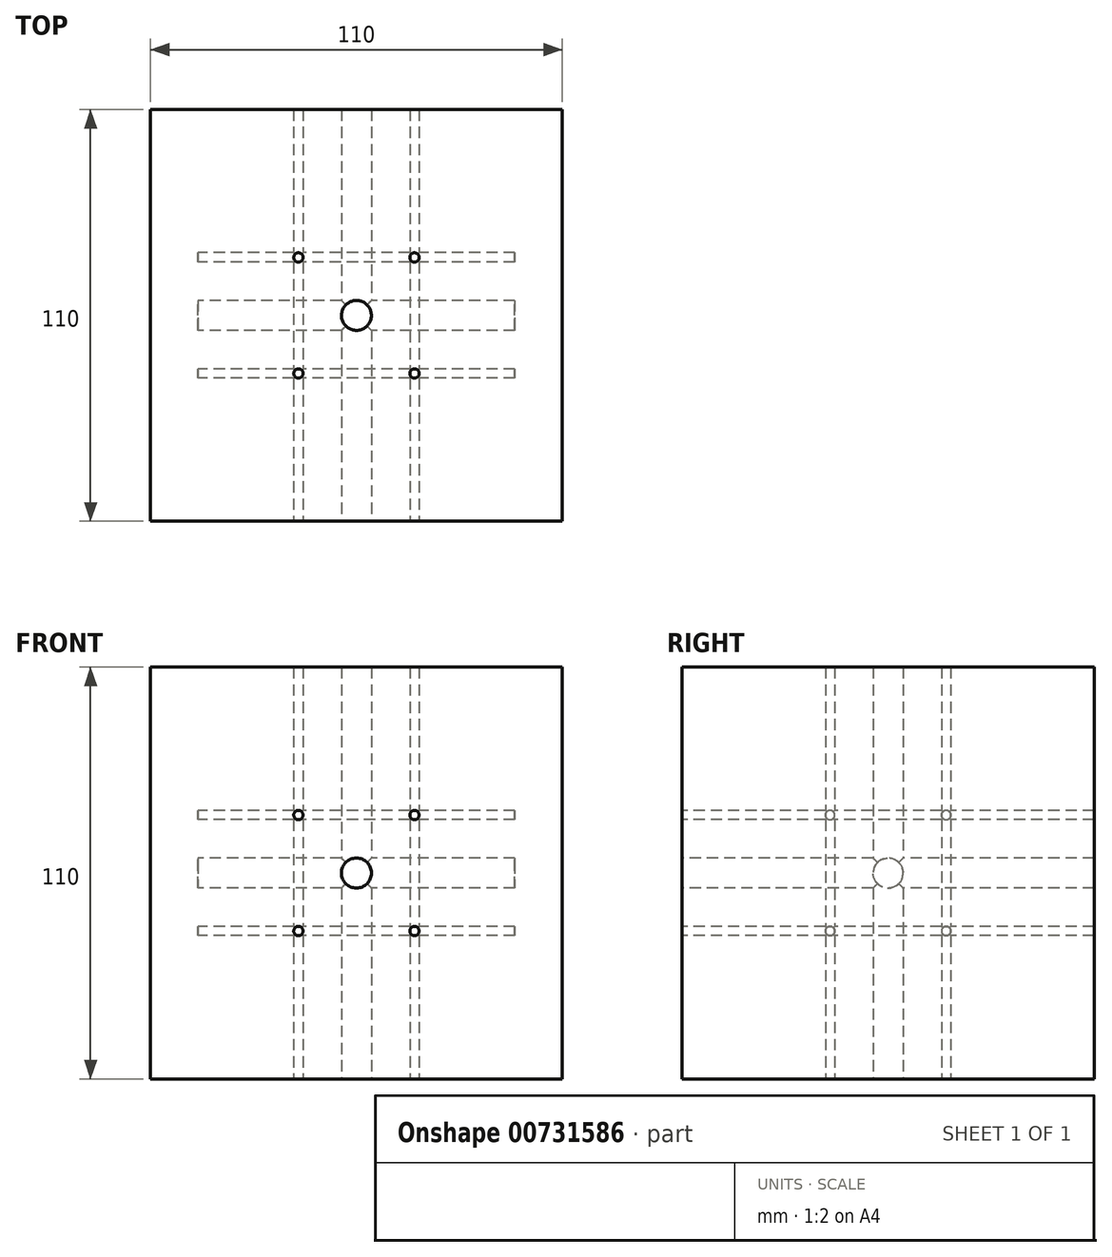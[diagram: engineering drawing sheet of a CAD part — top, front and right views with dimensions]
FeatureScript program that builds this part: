
annotation { "Feature Type Name" : "Feature", "Feature Type Description" : "" }
export const myFeature = defineFeature(function(context is Context, id is Id, definition is map)
    precondition{}
    {
        {
            assignVariable(context, id + "F0", {"name" : "MOT", "anyValue" : 42.3});
        }
        {
            var Q0;
            Q0=qCreatedBy(makeId("Top.planeOp"),FACE);
            var sketch = newSketch(context, id + "F1", { "sketchPlane" : qUnion([Q0])});
            skCircle(sketch, "E0.0", {"center": v(-15.5, 15.5) * mm, "radius": 1.25 * mm});
            skCircle(sketch, "E0.1", {"center": v(-15.5, -15.5) * mm, "radius": 1.25 * mm});
            skCircle(sketch, "E0.2", {"center": v(15.5, -15.5) * mm, "radius": 1.25 * mm});
            skCircle(sketch, "E0.3", {"center": v(15.5, 15.5) * mm, "radius": 1.25 * mm});
            skCircle(sketch, "E1", {"center": v(0, 0) * mm, "radius": 21.92 * mm, "construction": true});
            skLineSegment(sketch, "E2.bottom", {"start": v(55, 55) * mm, "end": v(-55, 55) * mm});
            skLineSegment(sketch, "E2.top", {"start": v(55, -55) * mm, "end": v(-55, -55) * mm});
            skLineSegment(sketch, "E2.left", {"start": v(55, 55) * mm, "end": v(55, -55) * mm});
            skLineSegment(sketch, "E2.right", {"start": v(-55, 55) * mm, "end": v(-55, -55) * mm});
            skLineSegment(sketch, "E3.bottom", {"start": v(21.15, 21.15) * mm, "end": v(-21.15, 21.15) * mm, "construction": true});
            skLineSegment(sketch, "E3.top", {"start": v(21.15, -21.15) * mm, "end": v(-21.15, -21.15) * mm, "construction": true});
            skLineSegment(sketch, "E3.left", {"start": v(21.15, 21.15) * mm, "end": v(21.15, -21.15) * mm, "construction": true});
            skLineSegment(sketch, "E3.right", {"start": v(-21.15, 21.15) * mm, "end": v(-21.15, -21.15) * mm, "construction": true});
            skCircle(sketch, "E4", {"center": v(0, 0) * mm, "radius": 55 * mm, "construction": true});
            skCircle(sketch, "E5", {"center": v(0, 0) * mm, "radius": 21.15 * mm, "construction": true});
            skCircle(sketch, "E6", {"center": v(0, 0) * mm, "radius": 4 * mm});
            skLineSegment(sketch, "E7", {"start": v(-75.61, 0) * mm, "end": v(74.32, 0) * mm, "construction": true});
            skSolve(sketch);
        }
        {
            var Q0;
            Q0=makeQuery(id+"F1.imprint","IMPRINT",FACE,{"disambiguationData":[TD([[makeQuery(id+"F1.imprint","IMPRINT",EDGE,{"derivedFrom":sQuery(id+"F1.wireOp",EDGE,"E0.0")}),-1.0]])]});
            extrude(context, id + "F2", {"entities" : qUnion([Q0]), "depth" : 110 * mm, "offsetDistance" : 25 * mm, "symmetric" : true});
        }
        {
            var Q0;
            Q0=qCreatedBy(makeId("Front.planeOp"),FACE);
            var sketch = newSketch(context, id + "F3", { "sketchPlane" : qUnion([Q0])});
            skCircle(sketch, "E8.0", {"center": v(-15.5, 15.5) * mm, "radius": 1.25 * mm});
            skCircle(sketch, "E8.1", {"center": v(-15.5, -15.5) * mm, "radius": 1.25 * mm});
            skCircle(sketch, "E8.2", {"center": v(15.5, -15.5) * mm, "radius": 1.25 * mm});
            skCircle(sketch, "E8.3", {"center": v(15.5, 15.5) * mm, "radius": 1.25 * mm});
            skCircle(sketch, "E9", {"center": v(0, 0) * mm, "radius": 21.92 * mm, "construction": true});
            skLineSegment(sketch, "E10.bottom", {"start": v(27.5, 27.5) * mm, "end": v(-27.5, 27.5) * mm});
            skLineSegment(sketch, "E10.top", {"start": v(27.5, -27.5) * mm, "end": v(-27.5, -27.5) * mm});
            skLineSegment(sketch, "E10.left", {"start": v(27.5, 27.5) * mm, "end": v(27.5, -27.5) * mm});
            skLineSegment(sketch, "E10.right", {"start": v(-27.5, 27.5) * mm, "end": v(-27.5, -27.5) * mm});
            skLineSegment(sketch, "E11.bottom", {"start": v(21.15, 21.15) * mm, "end": v(-21.15, 21.15) * mm, "construction": true});
            skLineSegment(sketch, "E11.top", {"start": v(21.15, -21.15) * mm, "end": v(-21.15, -21.15) * mm, "construction": true});
            skLineSegment(sketch, "E11.left", {"start": v(21.15, 21.15) * mm, "end": v(21.15, -21.15) * mm, "construction": true});
            skLineSegment(sketch, "E11.right", {"start": v(-21.15, 21.15) * mm, "end": v(-21.15, -21.15) * mm, "construction": true});
            skCircle(sketch, "E12", {"center": v(0, 0) * mm, "radius": 27.5 * mm, "construction": true});
            skCircle(sketch, "E13", {"center": v(0, 0) * mm, "radius": 21.15 * mm, "construction": true});
            skCircle(sketch, "E14", {"center": v(0, 0) * mm, "radius": 4 * mm});
            skLineSegment(sketch, "E15", {"start": v(-75.61, 0) * mm, "end": v(74.32, 0) * mm, "construction": true});
            skSolve(sketch);
        }
        {
            var Q0;
            Q0=makeQuery(id+"F3.imprint","IMPRINT",FACE,{"disambiguationData":[TD([[makeQuery(id+"F3.imprint","IMPRINT",EDGE,{"derivedFrom":sQuery(id+"F3.wireOp",EDGE,"E8.3")}),1.0]])]});
            var Q1;
            Q1=makeQuery(id+"F3.imprint","IMPRINT",FACE,{"disambiguationData":[TD([[makeQuery(id+"F3.imprint","IMPRINT",EDGE,{"derivedFrom":sQuery(id+"F3.wireOp",EDGE,"E14")}),1.0]])]});
            var Q2;
            Q2=makeQuery(id+"F3.imprint","IMPRINT",FACE,{"disambiguationData":[TD([[makeQuery(id+"F3.imprint","IMPRINT",EDGE,{"derivedFrom":sQuery(id+"F3.wireOp",EDGE,"E8.0")}),1.0]])]});
            var Q3;
            Q3=makeQuery(id+"F3.imprint","IMPRINT",FACE,{"disambiguationData":[TD([[makeQuery(id+"F3.imprint","IMPRINT",EDGE,{"derivedFrom":sQuery(id+"F3.wireOp",EDGE,"E8.1")}),1.0]])]});
            var Q4;
            Q4=makeQuery(id+"F3.imprint","IMPRINT",FACE,{"disambiguationData":[TD([[makeQuery(id+"F3.imprint","IMPRINT",EDGE,{"derivedFrom":sQuery(id+"F3.wireOp",EDGE,"E8.2")}),1.0]])]});
            extrude(context, id + "F4", {"entities" : qUnion([Q0, Q1, Q2, Q3, Q4]), "operationType" : NewBodyOperationType.REMOVE, "endBound" : BoundingType.THROUGH_ALL, "oppositeDirection" : true, "depth" : (getVariable(context, 'MOT') * 2) * mm, "offsetDistance" : 25 * mm, "hasSecondDirection" : true, "secondDirectionBound" : BoundingType.THROUGH_ALL, "secondDirectionOppositeDirection" : false, "secondDirectionDepth" : 25 * mm});
        }
        {
            var Q0;
            Q0=qCreatedBy(makeId("Right.planeOp"),FACE);
            var sketch = newSketch(context, id + "F5", { "sketchPlane" : qUnion([Q0])});
            skCircle(sketch, "E16.0", {"center": v(-15.5, 15.5) * mm, "radius": 1.25 * mm});
            skCircle(sketch, "E16.1", {"center": v(-15.5, -15.5) * mm, "radius": 1.25 * mm});
            skCircle(sketch, "E16.2", {"center": v(15.5, -15.5) * mm, "radius": 1.25 * mm});
            skCircle(sketch, "E16.3", {"center": v(15.5, 15.5) * mm, "radius": 1.25 * mm});
            skCircle(sketch, "E17", {"center": v(0, 0) * mm, "radius": 21.92 * mm, "construction": true});
            skLineSegment(sketch, "E18.bottom", {"start": v(27.5, 27.5) * mm, "end": v(-27.5, 27.5) * mm});
            skLineSegment(sketch, "E18.top", {"start": v(27.5, -27.5) * mm, "end": v(-27.5, -27.5) * mm});
            skLineSegment(sketch, "E18.left", {"start": v(27.5, 27.5) * mm, "end": v(27.5, -27.5) * mm});
            skLineSegment(sketch, "E18.right", {"start": v(-27.5, 27.5) * mm, "end": v(-27.5, -27.5) * mm});
            skLineSegment(sketch, "E19.bottom", {"start": v(21.15, 21.15) * mm, "end": v(-21.15, 21.15) * mm, "construction": true});
            skLineSegment(sketch, "E19.top", {"start": v(21.15, -21.15) * mm, "end": v(-21.15, -21.15) * mm, "construction": true});
            skLineSegment(sketch, "E19.left", {"start": v(21.15, 21.15) * mm, "end": v(21.15, -21.15) * mm, "construction": true});
            skLineSegment(sketch, "E19.right", {"start": v(-21.15, 21.15) * mm, "end": v(-21.15, -21.15) * mm, "construction": true});
            skCircle(sketch, "E20", {"center": v(0, 0) * mm, "radius": 27.5 * mm, "construction": true});
            skCircle(sketch, "E21", {"center": v(0, 0) * mm, "radius": 21.15 * mm, "construction": true});
            skCircle(sketch, "E22", {"center": v(0, 0) * mm, "radius": 4 * mm});
            skLineSegment(sketch, "E23", {"start": v(-75.61, 0) * mm, "end": v(74.32, 0) * mm, "construction": true});
            skSolve(sketch);
        }
        {
            var Q0;
            Q0=makeQuery(id+"F5.imprint","IMPRINT",FACE,{"disambiguationData":[TD([[makeQuery(id+"F5.imprint","IMPRINT",EDGE,{"derivedFrom":sQuery(id+"F5.wireOp",EDGE,"E16.0")}),1.0]])]});
            var Q1;
            Q1=makeQuery(id+"F5.imprint","IMPRINT",FACE,{"disambiguationData":[TD([[makeQuery(id+"F5.imprint","IMPRINT",EDGE,{"derivedFrom":sQuery(id+"F5.wireOp",EDGE,"E22")}),1.0]])]});
            var Q2;
            Q2=makeQuery(id+"F5.imprint","IMPRINT",FACE,{"disambiguationData":[TD([[makeQuery(id+"F5.imprint","IMPRINT",EDGE,{"derivedFrom":sQuery(id+"F5.wireOp",EDGE,"E16.3")}),1.0]])]});
            var Q3;
            Q3=makeQuery(id+"F5.imprint","IMPRINT",FACE,{"disambiguationData":[TD([[makeQuery(id+"F5.imprint","IMPRINT",EDGE,{"derivedFrom":sQuery(id+"F5.wireOp",EDGE,"E16.2")}),1.0]])]});
            var Q4;
            Q4=makeQuery(id+"F5.imprint","IMPRINT",FACE,{"disambiguationData":[TD([[makeQuery(id+"F5.imprint","IMPRINT",EDGE,{"derivedFrom":sQuery(id+"F5.wireOp",EDGE,"E16.1")}),1.0]])]});
            extrude(context, id + "F6", {"entities" : qUnion([Q0, Q1, Q2, Q3, Q4]), "operationType" : NewBodyOperationType.REMOVE, "depth" : (getVariable(context, 'MOT') * 2) * mm, "offsetDistance" : 25 * mm, "symmetric" : true});
        }
    });
